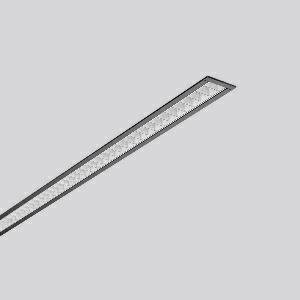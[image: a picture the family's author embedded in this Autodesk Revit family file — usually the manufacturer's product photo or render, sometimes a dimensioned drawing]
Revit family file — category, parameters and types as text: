
# Revit family: less_is_more_27_312179_003_ddca
name_source: partatom
category: Lighting Fixtures
units: mm (PartAtom-declared; Revit-internal decimal feet)

## family parameters
Cut with Voids When Loaded = No
Host = Face
Light Source = No
Part Type = Normal
Room Calculation Point = No
Round Connector Dimension = Use Diameter
Shared = No

## types (1)
- LESS IS MORE 27 (1 x LED Modul 830, 3500 lm, 3000)
    Apparent Load = 43 VA
    CIE Flux Codes = 90 99 100 100 100
    Color Rendering = 80
    Color Temperature = 3000
    Default Elevation = 1800 mm
    Description = Series: LESS IS MORE 27
Recessed ceiling and wall luminaire with slim design. Housing: extruded aluminium profile, powder-coated. End cap aluminium powder-coated. High polish aluminium micro grid. Perfect for office areas (RUG < 19) and environments with computer screens in accordance with EN 12464-1. Suitable for Recessed ceiling mounting, wall (recessed). External driver with connecting cable. 
Colour: deep black, matt (RAL 9005)
Length: 1514 mm
Width: 38 mm
Height: 2 mm
Cut-out length: 1506 mm
Cut-out width: 30 mm
Recess height: 45-60 mm
Luminaire: recess height: 37 mm
Lamp: LED
Socket: without socket
Colour temperature: 3000K
Colour rendering index (CRI): 82
System power: 43 W
Rated luminous flux: 3500 lm
Luminous efficiency: 81 lm/W
Control gear: Regulated power supply
Protection class: II
Type of protection: IP 20
    Height = 0 mm  [stored 0 ft]
    Lamp = 1 x LED Modul 830
    Lamp Light Flux = 3500 lm
    Lamp count = 1
    Length = 1514 mm
    Lifetime = 50000 h
    Luminous efficacy = 81 lm/W
    Manufacturer = RZB
    ModVariant = No
    Model = 312179.003
    Mounting Place = Ceiling, Wall
    Mounting Type = Recessed
    Number of Poles = 1
    OnlyDefault = Yes
    Power Factor = 1
    Product Name = LESS IS MORE 27
    Product group = Recessed LED linear luminaires
    ProductGroupID = 407
    Protection Class = Protection class II
    Protection Degree = IP 20
    RLX_Detail_Level = 1
    RLX_Emergency_Light_Flux = 0 lm
    RLX_Emergency_Type = 0
    RLX_Emergency_Type_DB = No
    RlxData = <blob elided: 29909 chars, md5=31abe605>
    Socket = socket
    Standby Power = 0 W
    System Light Flux = 3500 lm
    System Power = 43 W
    Type Comments = Product without accessories
    Type Image = 312177.003.jpg
    URL = http://relux.com
    VarID = ---
    Voltage = 230 V
    Voltage Range = 220-240 V
    Weight = 0.00 kg
    Width = 38 mm

note: [stored X ft] marks values corroborated as IEEE doubles in the binary element streams (Revit-internal decimal feet)

## geometry (parser evidence)
native form markers: Blend x4, Sweep x10
no freeform markers — native parametric forms only
